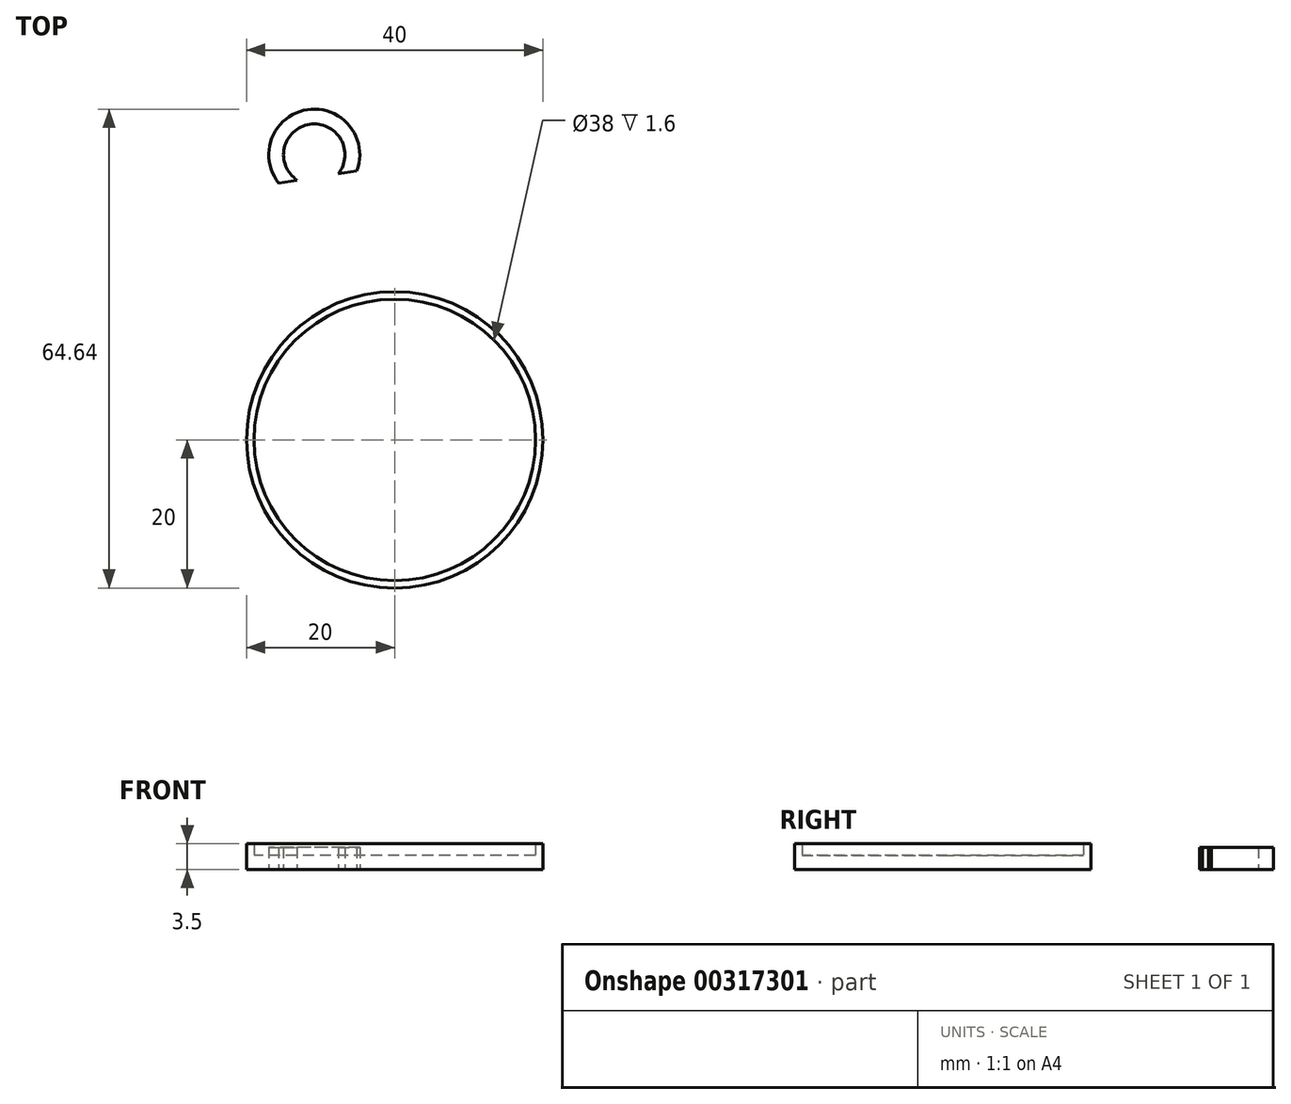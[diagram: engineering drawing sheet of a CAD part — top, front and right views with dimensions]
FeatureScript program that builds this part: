
annotation { "Feature Type Name" : "Feature", "Feature Type Description" : "" }
export const myFeature = defineFeature(function(context is Context, id is Id, definition is map)
    precondition{}
    {
        {
            var Q0;
            Q0=qCreatedBy(makeId("Top.planeOp"),FACE);
            var sketch = newSketch(context, id + "F0", { "sketchPlane" : qUnion([Q0])});
            skCircle(sketch, "E0", {"center": v(0, 0) * mm, "radius": 20 * mm});
            skSolve(sketch);
        }
        {
            var Q0;
            Q0 = qSketchRegion(id + "F0", true);
            extrude(context, id + "F1", {"entities" : qUnion([Q0]), "depth" : 3.5 * mm});
        }
        {
            var Q0;
            Q0=makeQuery(id+"F1.opExtrude","CAP_FACE",FACE,{"disambiguationData":[OSD([sQuery(id+"F0.wireOp",EDGE,"E0")])],"isStart":false});
            shell(context, id + "F2", {"entities" : qUnion([Q0]), "thickness" : 1 * mm});
        }
        {
            var Q0;
            {var subQ0=sQuery(id+"F0.wireOp",EDGE,"E0");Q0=makeQuery(id+"F2.opShell","OFFSET_FACE",FACE,{"disambiguationData":[OSD([subQ0]),TDD([makeQuery(id+"F1.opExtrude","CAP_FACE",FACE,{"disambiguationData":[OSD([subQ0])],"isStart":true})])]});}
            extrude(context, id + "F3", {"entities" : qUnion([Q0]), "operationType" : NewBodyOperationType.ADD, "depth" : 0.9 * mm});
        }
        {
            var Q0;
            Q0=qCreatedBy(makeId("Top.planeOp"),FACE);
            var sketch = newSketch(context, id + "F4", { "sketchPlane" : qUnion([Q0])});
            skCircle(sketch, "E1", {"center": v(-10.86, 38.5) * mm, "radius": 6.15 * mm});
            skLineSegment(sketch, "E2", {"start": v(-21.43, 33.79) * mm, "end": v(2.03, 37.4) * mm});
            skSolve(sketch);
        }
        {
            var Q0;
            Q0=makeQuery(id+"F4.imprint","IMPRINT",FACE,{"disambiguationData":[TD([[makeQuery(id+"F4.imprint","IMPRINT",EDGE,{"derivedFrom":sQuery(id+"F4.wireOp",EDGE,"E1")}),1.0]])]});
            extrude(context, id + "F5", {"entities" : qUnion([Q0]), "depth" : 3 * mm});
        }
        {
            var Q0;
            Q0=makeQuery(id+"F5.opExtrude","CAP_FACE",FACE,{"disambiguationData":[OSD([sQuery(id+"F4.wireOp",EDGE,"E1")])],"isStart":false});
            shell(context, id + "F6", {"entities" : qUnion([Q0]), "thickness" : 2 * mm});
        }
        {
            var Q0;
            {var subQ0=sQuery(id+"F4.wireOp",EDGE,"E1");Q0=makeQuery(id+"F6.opShell","OFFSET_FACE",FACE,{"disambiguationData":[OSD([subQ0]),TDD([makeQuery(id+"F5.opExtrude","CAP_FACE",FACE,{"disambiguationData":[OSD([subQ0])],"isStart":true})])]});}
            extrude(context, id + "F7", {"entities" : qUnion([Q0]), "operationType" : NewBodyOperationType.REMOVE, "oppositeDirection" : true, "depth" : 25 * mm});
        }
        {
            var Q0;
            Q0=sQuery(id+"F4.wireOp",EDGE,"E2");
            extrude(context, id + "F8", {"bodyType" : ToolBodyType.SURFACE, "operationType" : NewBodyOperationType.INTERSECT, "surfaceEntities" : qUnion([Q0]), "endBound" : BoundingType.SYMMETRIC, "depth" : 19.7 * mm});
        }
        {
            var Q0;
            Q0=makeQuery(id+"F8.opExtrude","SWEPT_FACE",FACE,{"disambiguationData":[OSD([sQuery(id+"F4.wireOp",EDGE,"E2")])]});
            extrude(context, id + "F9", {"entities" : qUnion([Q0]), "operationType" : NewBodyOperationType.REMOVE, "depth" : 3.6 * mm});
        }
    });
